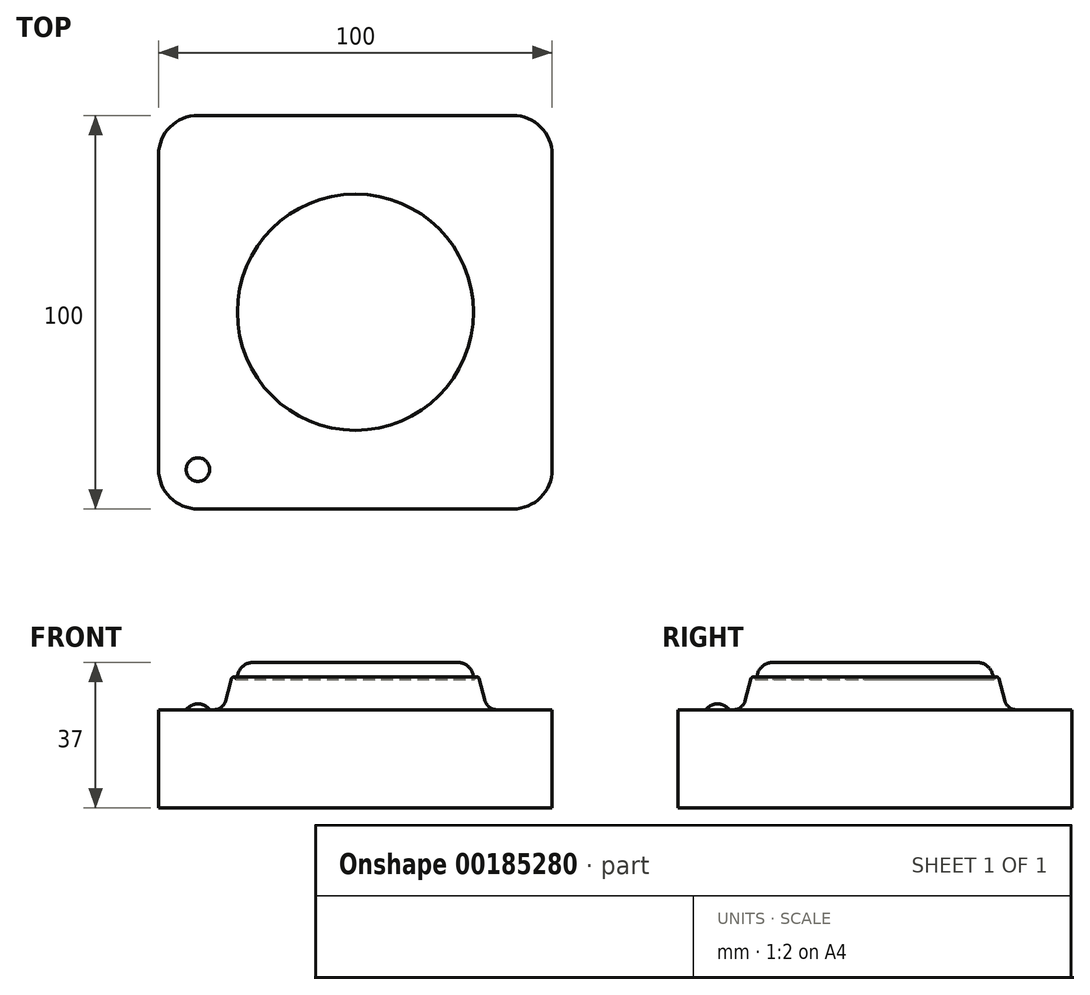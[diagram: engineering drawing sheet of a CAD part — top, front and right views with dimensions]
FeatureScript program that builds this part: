
annotation { "Feature Type Name" : "Feature", "Feature Type Description" : "" }
export const myFeature = defineFeature(function(context is Context, id is Id, definition is map)
    precondition{}
    {
        {
            var Q0;
            Q0=qCreatedBy(makeId("Top.planeOp"),FACE);
            var sketch = newSketch(context, id + "F0", { "sketchPlane" : qUnion([Q0])});
            skLineSegment(sketch, "E0.bottom", {"start": v(40, 50) * mm, "end": v(-40, 50) * mm});
            skLineSegment(sketch, "E0.top", {"start": v(40, -50) * mm, "end": v(-40, -50) * mm});
            skLineSegment(sketch, "E0.left", {"start": v(50, 40) * mm, "end": v(50, -40) * mm});
            skLineSegment(sketch, "E0.right", {"start": v(-50, 40) * mm, "end": v(-50, -40) * mm});
            skPoint(sketch, "E0.middle", {"position": v(0, 0) * mm});
            skPoint(sketch, "E1.visualSharp", {"position": v(-50, -50) * mm});
            skArc(sketch, "E1.filletArc", {"start": v(-50, -40) * mm, "mid": v(-47.07, -47.07) * mm, "end": v(-40, -50) * mm});
            skPoint(sketch, "E2.visualSharp", {"position": v(-50, 50) * mm});
            skArc(sketch, "E2.filletArc", {"start": v(-40, 50) * mm, "mid": v(-47.07, 47.07) * mm, "end": v(-50, 40) * mm});
            skPoint(sketch, "E3.visualSharp", {"position": v(50, 50) * mm});
            skArc(sketch, "E3.filletArc", {"start": v(50, 40) * mm, "mid": v(47.07, 47.07) * mm, "end": v(40, 50) * mm});
            skPoint(sketch, "E4.visualSharp", {"position": v(50, -50) * mm});
            skArc(sketch, "E4.filletArc", {"start": v(40, -50) * mm, "mid": v(47.07, -47.07) * mm, "end": v(50, -40) * mm});
            skSolve(sketch);
        }
        {
            var Q0;
            Q0 = qSketchRegion(id + "F0", true);
            extrude(context, id + "F1", {"entities" : qUnion([Q0]), "depth" : 25 * mm});
        }
        {
            var Q0;
            Q0=qCreatedBy(makeId("Front.planeOp"),FACE);
            var sketch = newSketch(context, id + "F2", { "sketchPlane" : qUnion([Q0])});
            skLineSegment(sketch, "E5", {"start": v(0, 0) * mm, "end": v(0, 64.09) * mm, "construction": true});
            skLineSegment(sketch, "E6", {"start": v(0, 37) * mm, "end": v(26, 37) * mm});
            skArc(sketch, "E7", {"start": v(26, 37) * mm, "mid": v(28.83, 35.83) * mm, "end": v(30, 33) * mm});
            skArc(sketch, "E8", {"start": v(30, 33) * mm, "mid": v(30.22, 32.75) * mm, "end": v(30.5, 32.94) * mm});
            skArc(sketch, "E9", {"start": v(30.5, 32.94) * mm, "mid": v(30.97, 33.3) * mm, "end": v(31.46, 32.94) * mm});
            skLineSegment(sketch, "E10", {"start": v(31.46, 32.94) * mm, "end": v(32.99, 27.22) * mm});
            skArc(sketch, "E11", {"start": v(32.99, 27.22) * mm, "mid": v(34.06, 25.62) * mm, "end": v(35.89, 25) * mm});
            skLineSegment(sketch, "E12", {"start": v(35.89, 25) * mm, "end": v(0, 25) * mm});
            skLineSegment(sketch, "E13", {"start": v(0, 37) * mm, "end": v(0, 25) * mm});
            skSolve(sketch);
        }
        {
            var Q0;
            Q0=makeQuery(id+"F2.imprint","IMPRINT",FACE,{"disambiguationData":[TD([[makeQuery(id+"F2.imprint","IMPRINT",EDGE,{"derivedFrom":sQuery(id+"F2.wireOp",EDGE,"E6")}),-1.0]])]});
            var Q1;
            Q1=sQuery(id+"F2.wireOp",EDGE,"E5");
            revolve(context, id + "F3", {"operationType" : NewBodyOperationType.ADD, "entities" : qUnion([Q0]), "axis" : qUnion([Q1]), "revolveType" : RevolveType.FULL});
        }
        {
            var Q0;
            Q0=qCreatedBy(makeId("Front.planeOp"),FACE);
            var Q1;
            Q1=makeQuery(id+"F1.opExtrude","CAP_VERTEX",VERTEX,{"disambiguationData":[OSD([sQuery(id+"F0.wireOp",EDGE,"E0.right"),sQuery(id+"F0.wireOp",EDGE,"E1.filletArc")])],"isStart":false});
            cPlane(context, id + "F4", {"entities" : qUnion([Q0, Q1]), "cplaneType" : CPlaneType.PLANE_POINT, "offset" : 25 * mm, "width" : 150 * mm, "height" : 150 * mm});
        }
        {
            var Q0;
            Q0=qCreatedBy(id+"F4.planeOp",FACE);
            var sketch = newSketch(context, id + "F5", { "sketchPlane" : qUnion([Q0])});
            skLineSegment(sketch, "E14", {"start": v(-40, 25) * mm, "end": v(-40, 39) * mm, "construction": true});
            skLineSegment(sketch, "E15", {"start": v(-40, 25) * mm, "end": v(-37, 25) * mm});
            skLineSegment(sketch, "E16", {"start": v(-40, 25) * mm, "end": v(-40, 26.5) * mm});
            skArc(sketch, "E17", {"start": v(-37, 25) * mm, "mid": v(-38.32, 26.1) * mm, "end": v(-40, 26.5) * mm});
            skSolve(sketch);
        }
        {
            var Q0;
            Q0=makeQuery(id+"F5.imprint","IMPRINT",FACE,{"disambiguationData":[TD([[makeQuery(id+"F5.imprint","IMPRINT",EDGE,{"derivedFrom":sQuery(id+"F5.wireOp",EDGE,"E15")}),1.0]])]});
            var Q1;
            Q1=sQuery(id+"F5.wireOp",EDGE,"E14");
            revolve(context, id + "F6", {"operationType" : NewBodyOperationType.ADD, "entities" : qUnion([Q0]), "axis" : qUnion([Q1]), "revolveType" : RevolveType.FULL});
        }
    });
